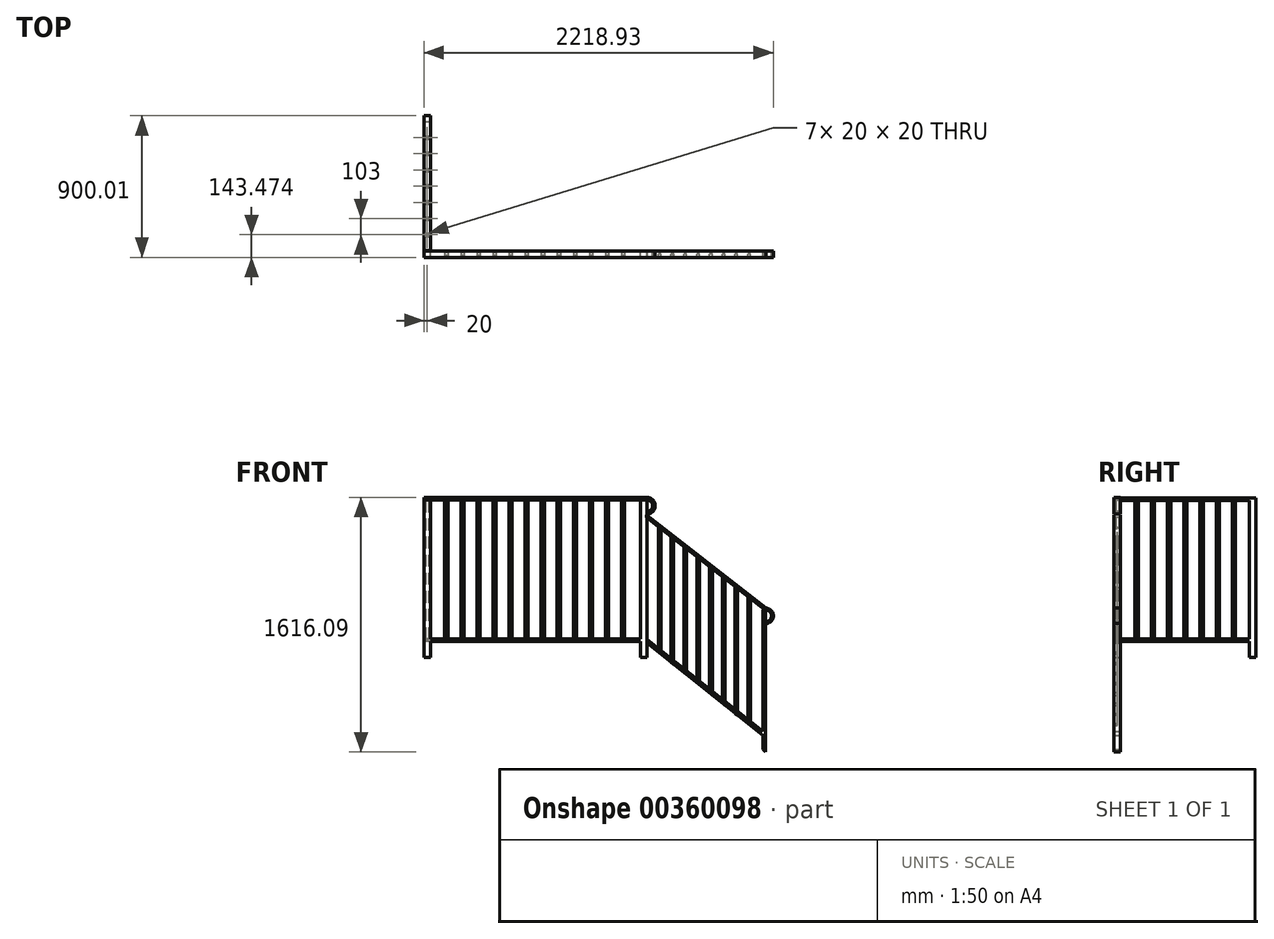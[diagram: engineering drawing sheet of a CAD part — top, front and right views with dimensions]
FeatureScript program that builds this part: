
annotation { "Feature Type Name" : "Feature", "Feature Type Description" : "" }
export const myFeature = defineFeature(function(context is Context, id is Id, definition is map)
    precondition{}
    {
        {
            var Q0;
            Q0=qCreatedBy(makeId("Front.planeOp"),FACE);
            var sketch = newSketch(context, id + "F0", { "sketchPlane" : qUnion([Q0])});
            skLineSegment(sketch, "E0", {"start": v(1415, 600.1) * mm, "end": v(1415, 1600.1) * mm});
            skLineSegment(sketch, "E1", {"start": v(1415, 1600.1) * mm, "end": v(1375, 1600.1) * mm});
            skLineSegment(sketch, "E2", {"start": v(1375, 1600.1) * mm, "end": v(1375, 600.14) * mm});
            skLineSegment(sketch, "E3", {"start": v(1375, 600.14) * mm, "end": v(1415, 600.1) * mm});
            skLineSegment(sketch, "E4.bottom", {"start": v(0, 600.1) * mm, "end": v(40, 600.1) * mm});
            skLineSegment(sketch, "E4.top", {"start": v(0, 1600.1) * mm, "end": v(40, 1600.1) * mm});
            skLineSegment(sketch, "E4.left", {"start": v(0, 600.1) * mm, "end": v(0, 1600.1) * mm});
            skLineSegment(sketch, "E4.right", {"start": v(40, 600.1) * mm, "end": v(40, 1600.1) * mm});
            skLineSegment(sketch, "E5", {"start": v(40, 600.1) * mm, "end": v(40, 700.1) * mm});
            skLineSegment(sketch, "E6", {"start": v(40, 700.1) * mm, "end": v(1375, 700.1) * mm});
            skLineSegment(sketch, "E7", {"start": v(1375, 700.1) * mm, "end": v(1375, 716.1) * mm});
            skLineSegment(sketch, "E8", {"start": v(1375, 716.1) * mm, "end": v(40, 716.1) * mm});
            skLineSegment(sketch, "E9", {"start": v(40, 716.1) * mm, "end": v(40, 700.1) * mm});
            skSolve(sketch);
        }
        {
            var Q0;
            Q0 = qSketchRegion(id + "F0", true);
            extrude(context, id + "F1", {"entities" : qUnion([Q0]), "endBound" : BoundingType.SYMMETRIC, "depth" : 40 * mm});
        }
        {
            var Q0;
            Q0=makeQuery(id+"F1.opExtrude","SWEPT_FACE",FACE,{"disambiguationData":[OSD([sQuery(id+"F0.wireOp",EDGE,"E4.left")])]});
            var sketch = newSketch(context, id + "F2", { "sketchPlane" : qUnion([Q0])});
            skLineSegment(sketch, "E10.bottom", {"start": v(-20, 1600.1) * mm, "end": v(20, 1600.1) * mm});
            skLineSegment(sketch, "E10.top", {"start": v(-20, 1616.1) * mm, "end": v(20, 1616.1) * mm});
            skLineSegment(sketch, "E10.left", {"start": v(-20, 1600.1) * mm, "end": v(-20, 1616.1) * mm});
            skLineSegment(sketch, "E10.right", {"start": v(20, 1600.1) * mm, "end": v(20, 1616.1) * mm});
            skSolve(sketch);
        }
        {
            var Q0;
            Q0=makeQuery(id+"F2.imprint","IMPRINT",FACE,{"disambiguationData":[TD([[makeQuery(id+"F2.imprint","IMPRINT",EDGE,{"derivedFrom":sQuery(id+"F2.wireOp",EDGE,"E10.bottom")}),-1.0]])]});
            var sketch = newSketch(context, id + "F3", { "sketchPlane" : qUnion([Q0])});
            skLineSegment(sketch, "E11.bottom", {"start": v(-20, 1600.2) * mm, "end": v(20, 1600.2) * mm});
            skLineSegment(sketch, "E11.top", {"start": v(-20, 1616.2) * mm, "end": v(20, 1616.2) * mm});
            skLineSegment(sketch, "E11.left", {"start": v(-20, 1600.2) * mm, "end": v(-20, 1616.2) * mm});
            skLineSegment(sketch, "E11.right", {"start": v(20, 1600.2) * mm, "end": v(20, 1616.2) * mm});
            skPoint(sketch, "E11.middle", {"position": v(0, 1608.2) * mm});
            skSolve(sketch);
        }
        {
            var Q0;
            Q0=qCreatedBy(makeId("Front.planeOp"),FACE);
            var sketch = newSketch(context, id + "F4", { "sketchPlane" : qUnion([Q0])});
            skLineSegment(sketch, "E12", {"start": v(0, 1608.38) * mm, "end": v(1415.74, 1608.38) * mm});
            skArc(sketch, "E13", {"start": v(1415.74, 1518.38) * mm, "mid": v(1460.74, 1563.38) * mm, "end": v(1415.74, 1608.38) * mm});
            skSolve(sketch);
        }
        {
            var Q0;
            {var subQ0=sQuery(id+"F3.wireOp",EDGE,"E11.left");var subQ1=sQuery(id+"F3.wireOp",EDGE,"E11.bottom");var subQ2=makeQuery(id+"F3.imprint","INTERSECT",VERTEX,{"derivedFrom":[subQ1,subQ0]});Q0=makeQuery(id+"F3.imprint","IMPRINT",FACE,{"disambiguationData":[TD([[makeQuery(id+"F3.imprint","IMPRINT",EDGE,{"disambiguationData":[TD([[subQ2,-1.0]])],"derivedFrom":subQ1}),1.0]])]});}
            var Q1;
            Q1=sQuery(id+"F4.wireOp",EDGE,"E12");
            var Q2;
            Q2=sQuery(id+"F4.wireOp",EDGE,"E13");
            sweep(context, id + "F5", {"profiles" : qUnion([Q0]), "path" : qUnion([Q1, Q2])});
        }
        {
            var Q0;
            Q0=qCreatedBy(makeId("Front.planeOp"),FACE);
            var sketch = newSketch(context, id + "F6", { "sketchPlane" : qUnion([Q0])});
            skLineSegment(sketch, "E14", {"start": v(2169.22, 0) * mm, "end": v(2169.22, 900) * mm});
            skLineSegment(sketch, "E15", {"start": v(1415.57, 1482.12) * mm, "end": v(1415.57, 1502.33) * mm});
            skLineSegment(sketch, "E16", {"start": v(2169.22, 900) * mm, "end": v(2153.22, 900) * mm});
            skLineSegment(sketch, "E17", {"start": v(2153.22, 900) * mm, "end": v(2153.22, 15.7) * mm});
            skLineSegment(sketch, "E18", {"start": v(2153.22, 15.7) * mm, "end": v(2169.22, 0) * mm});
            skLineSegment(sketch, "E19", {"start": v(1415.57, 692.8) * mm, "end": v(2153.22, 103.74) * mm});
            skLineSegment(sketch, "E20", {"start": v(1415.18, 712.76) * mm, "end": v(2153.22, 128.7) * mm});
            skLineSegment(sketch, "E21", {"start": v(1415.18, 712.76) * mm, "end": v(1415.57, 692.8) * mm});
            skSolve(sketch);
        }
        {
            var Q0;
            Q0 = qSketchRegion(id + "F6", true);
            extrude(context, id + "F7", {"entities" : qUnion([Q0]), "endBound" : BoundingType.SYMMETRIC, "depth" : 40 * mm});
        }
        {
            var Q0;
            Q0=makeQuery(id+"F1.opExtrude","SWEPT_FACE",FACE,{"disambiguationData":[OSD([sQuery(id+"F0.wireOp",EDGE,"E0")])]});
            var sketch = newSketch(context, id + "F8", { "sketchPlane" : qUnion([Q0])});
            skLineSegment(sketch, "E22.bottom", {"start": v(20, 1486.8) * mm, "end": v(-20, 1486.8) * mm});
            skLineSegment(sketch, "E22.top", {"start": v(20, 1502.8) * mm, "end": v(-20, 1502.8) * mm});
            skLineSegment(sketch, "E22.left", {"start": v(20, 1486.8) * mm, "end": v(20, 1502.8) * mm});
            skLineSegment(sketch, "E22.right", {"start": v(-20, 1486.8) * mm, "end": v(-20, 1502.8) * mm});
            skPoint(sketch, "E22.middle", {"position": v(0, 1494.8) * mm});
            skSolve(sketch);
        }
        {
            var Q0;
            Q0=qCreatedBy(makeId("Front.planeOp"),FACE);
            var sketch = newSketch(context, id + "F9", { "sketchPlane" : qUnion([Q0])});
            skLineSegment(sketch, "E23", {"start": v(2169.44, 908.95) * mm, "end": v(1413.58, 1498.8) * mm});
            skArc(sketch, "E24", {"start": v(2169.44, 818.95) * mm, "mid": v(2214.81, 863.95) * mm, "end": v(2169.44, 908.95) * mm});
            skSolve(sketch);
        }
        {
            var Q0;
            Q0=makeQuery(id+"F8.imprint","IMPRINT",FACE,{"disambiguationData":[TD([[makeQuery(id+"F8.imprint","IMPRINT",EDGE,{"derivedFrom":sQuery(id+"F8.wireOp",EDGE,"E22.bottom")}),-1.0]])]});
            var Q1;
            Q1=sQuery(id+"F9.wireOp",EDGE,"E23");
            var Q2;
            Q2=sQuery(id+"F9.wireOp",EDGE,"E24");
            sweep(context, id + "F10", {"profiles" : qUnion([Q0]), "path" : qUnion([Q1, Q2])});
        }
        {
            var Q0;
            Q0=makeQuery(id+"F1.opExtrude","SWEPT_FACE",FACE,{"disambiguationData":[OSD([sQuery(id+"F0.wireOp",EDGE,"E6")])]});
            var sketch = newSketch(context, id + "F11", { "sketchPlane" : qUnion([Q0])});
            skLineSegment(sketch, "E25", {"start": v(40, 0) * mm, "end": v(142, 0) * mm});
            skPoint(sketch, "E25.endSnap0", {"position": v(40, 0) * mm});
            skLineSegment(sketch, "E26", {"start": v(142, 0) * mm, "end": v(244, 0) * mm});
            skLineSegment(sketch, "E27", {"start": v(244, 0) * mm, "end": v(346, 0) * mm});
            skLineSegment(sketch, "E28", {"start": v(346, 0) * mm, "end": v(448, 0) * mm});
            skLineSegment(sketch, "E29", {"start": v(448, 0) * mm, "end": v(550, 0) * mm});
            skLineSegment(sketch, "E30", {"start": v(550, 0) * mm, "end": v(652, 0) * mm});
            skLineSegment(sketch, "E31", {"start": v(652, 0) * mm, "end": v(754, 0) * mm});
            skLineSegment(sketch, "E32", {"start": v(754, 0) * mm, "end": v(856, 0) * mm});
            skLineSegment(sketch, "E33", {"start": v(856, 0) * mm, "end": v(958, 0) * mm});
            skLineSegment(sketch, "E34", {"start": v(958, 0) * mm, "end": v(1060, 0) * mm});
            skLineSegment(sketch, "E35", {"start": v(1060, 0) * mm, "end": v(1162, 0) * mm});
            skLineSegment(sketch, "E36", {"start": v(1162, 0) * mm, "end": v(1264, 0) * mm});
            skLineSegment(sketch, "E37.bottom", {"start": v(152, -10) * mm, "end": v(132, -10) * mm});
            skLineSegment(sketch, "E37.top", {"start": v(152, 10) * mm, "end": v(132, 10) * mm});
            skLineSegment(sketch, "E37.left", {"start": v(152, -10) * mm, "end": v(152, 10) * mm});
            skLineSegment(sketch, "E37.right", {"start": v(132, -10) * mm, "end": v(132, 10) * mm});
            skPoint(sketch, "E37.middle", {"position": v(142, 0) * mm});
            skLineSegment(sketch, "E38.bottom", {"start": v(254, -10) * mm, "end": v(234, -10) * mm});
            skLineSegment(sketch, "E38.top", {"start": v(254, 10) * mm, "end": v(234, 10) * mm});
            skLineSegment(sketch, "E38.left", {"start": v(254, -10) * mm, "end": v(254, 10) * mm});
            skLineSegment(sketch, "E38.right", {"start": v(234, -10) * mm, "end": v(234, 10) * mm});
            skPoint(sketch, "E38.middle", {"position": v(244, 0) * mm});
            skLineSegment(sketch, "E39.bottom", {"start": v(356, -10) * mm, "end": v(336, -10) * mm});
            skLineSegment(sketch, "E39.top", {"start": v(356, 10) * mm, "end": v(336, 10) * mm});
            skLineSegment(sketch, "E39.left", {"start": v(356, -10) * mm, "end": v(356, 10) * mm});
            skLineSegment(sketch, "E39.right", {"start": v(336, -10) * mm, "end": v(336, 10) * mm});
            skPoint(sketch, "E39.middle", {"position": v(346, 0) * mm});
            skLineSegment(sketch, "E40.bottom", {"start": v(458, -10) * mm, "end": v(438, -10) * mm});
            skLineSegment(sketch, "E40.top", {"start": v(458, 10) * mm, "end": v(438, 10) * mm});
            skLineSegment(sketch, "E40.left", {"start": v(458, -10) * mm, "end": v(458, 10) * mm});
            skLineSegment(sketch, "E40.right", {"start": v(438, -10) * mm, "end": v(438, 10) * mm});
            skPoint(sketch, "E40.middle", {"position": v(448, 0) * mm});
            skLineSegment(sketch, "E41.bottom", {"start": v(560, -10) * mm, "end": v(540, -10) * mm});
            skLineSegment(sketch, "E41.top", {"start": v(560, 10) * mm, "end": v(540, 10) * mm});
            skLineSegment(sketch, "E41.left", {"start": v(560, -10) * mm, "end": v(560, 10) * mm});
            skLineSegment(sketch, "E41.right", {"start": v(540, -10) * mm, "end": v(540, 10) * mm});
            skPoint(sketch, "E41.middle", {"position": v(550, 0) * mm});
            skLineSegment(sketch, "E42.bottom", {"start": v(662, -10) * mm, "end": v(642, -10) * mm});
            skLineSegment(sketch, "E42.top", {"start": v(662, 10) * mm, "end": v(642, 10) * mm});
            skLineSegment(sketch, "E42.left", {"start": v(662, -10) * mm, "end": v(662, 10) * mm});
            skLineSegment(sketch, "E42.right", {"start": v(642, -10) * mm, "end": v(642, 10) * mm});
            skPoint(sketch, "E42.middle", {"position": v(652, 0) * mm});
            skLineSegment(sketch, "E43.bottom", {"start": v(764, -10) * mm, "end": v(744, -10) * mm});
            skLineSegment(sketch, "E43.top", {"start": v(764, 10) * mm, "end": v(744, 10) * mm});
            skLineSegment(sketch, "E43.left", {"start": v(764, -10) * mm, "end": v(764, 10) * mm});
            skLineSegment(sketch, "E43.right", {"start": v(744, -10) * mm, "end": v(744, 10) * mm});
            skPoint(sketch, "E43.middle", {"position": v(754, 0) * mm});
            skLineSegment(sketch, "E44.bottom", {"start": v(866, -10) * mm, "end": v(846, -10) * mm});
            skLineSegment(sketch, "E44.top", {"start": v(866, 10) * mm, "end": v(846, 10) * mm});
            skLineSegment(sketch, "E44.left", {"start": v(866, -10) * mm, "end": v(866, 10) * mm});
            skLineSegment(sketch, "E44.right", {"start": v(846, -10) * mm, "end": v(846, 10) * mm});
            skPoint(sketch, "E44.middle", {"position": v(856, 0) * mm});
            skLineSegment(sketch, "E45.bottom", {"start": v(968, -10) * mm, "end": v(948, -10) * mm});
            skLineSegment(sketch, "E45.top", {"start": v(968, 10) * mm, "end": v(948, 10) * mm});
            skLineSegment(sketch, "E45.left", {"start": v(968, -10) * mm, "end": v(968, 10) * mm});
            skLineSegment(sketch, "E45.right", {"start": v(948, -10) * mm, "end": v(948, 10) * mm});
            skPoint(sketch, "E45.middle", {"position": v(958, 0) * mm});
            skPoint(sketch, "E46.middle", {"position": v(1060, 0) * mm});
            skLineSegment(sketch, "E47.bottom", {"start": v(1070, -10) * mm, "end": v(1050, -10) * mm});
            skLineSegment(sketch, "E47.top", {"start": v(1070, 10) * mm, "end": v(1050, 10) * mm});
            skLineSegment(sketch, "E47.left", {"start": v(1070, -10) * mm, "end": v(1070, 10) * mm});
            skLineSegment(sketch, "E47.right", {"start": v(1050, -10) * mm, "end": v(1050, 10) * mm});
            skLineSegment(sketch, "E48.bottom", {"start": v(1172, -10) * mm, "end": v(1152, -10) * mm});
            skLineSegment(sketch, "E48.top", {"start": v(1172, 10) * mm, "end": v(1152, 10) * mm});
            skLineSegment(sketch, "E48.left", {"start": v(1172, -10) * mm, "end": v(1172, 10) * mm});
            skLineSegment(sketch, "E48.right", {"start": v(1152, -10) * mm, "end": v(1152, 10) * mm});
            skPoint(sketch, "E48.middle", {"position": v(1162, 0) * mm});
            skLineSegment(sketch, "E49.bottom", {"start": v(1274, -10) * mm, "end": v(1254, -10) * mm});
            skLineSegment(sketch, "E49.top", {"start": v(1274, 10) * mm, "end": v(1254, 10) * mm});
            skLineSegment(sketch, "E49.left", {"start": v(1274, -10) * mm, "end": v(1274, 10) * mm});
            skLineSegment(sketch, "E49.right", {"start": v(1254, -10) * mm, "end": v(1254, 10) * mm});
            skPoint(sketch, "E49.middle", {"position": v(1264, 0) * mm});
            skSolve(sketch);
        }
        {
            var Q0;
            Q0 = qSketchRegion(id + "F11", true);
            extrude(context, id + "F12", {"entities" : qUnion([Q0]), "oppositeDirection" : true, "depth" : 905 * mm});
        }
        {
            var Q0;
            Q0=qCreatedBy(makeId("Front.planeOp"),FACE);
            var sketch = newSketch(context, id + "F13", { "sketchPlane" : qUnion([Q0])});
            skLineSegment(sketch, "E50", {"start": v(1489.6, 633.32) * mm, "end": v(1489.6, 1429.3) * mm});
            skLineSegment(sketch, "E51", {"start": v(1504.3, 620.7) * mm, "end": v(1504.3, 1417.72) * mm});
            skLineSegment(sketch, "E52", {"start": v(1569.3, 568.65) * mm, "end": v(1569.3, 1361.75) * mm});
            skLineSegment(sketch, "E53", {"start": v(1585.39, 555.75) * mm, "end": v(1585.39, 1345.38) * mm});
            skLineSegment(sketch, "E54", {"start": v(1649.77, 505.44) * mm, "end": v(1649.77, 1302.64) * mm});
            skLineSegment(sketch, "E55", {"start": v(1667.4, 491.46) * mm, "end": v(1667.4, 1288.96) * mm});
            skLineSegment(sketch, "E56", {"start": v(1732.41, 440.66) * mm, "end": v(1732.41, 1239) * mm});
            skLineSegment(sketch, "E57", {"start": v(1748.8, 427.08) * mm, "end": v(1748.8, 1225.67) * mm});
            skLineSegment(sketch, "E58", {"start": v(1812.2, 377.07) * mm, "end": v(1812.2, 1175.59) * mm});
            skLineSegment(sketch, "E59", {"start": v(1831.2, 359.05) * mm, "end": v(1831.2, 1161.81) * mm});
            skLineSegment(sketch, "E60", {"start": v(1895.34, 310.04) * mm, "end": v(1895.34, 1111.73) * mm});
            skLineSegment(sketch, "E61", {"start": v(1910.53, 294.03) * mm, "end": v(1910.53, 1100.16) * mm});
            skLineSegment(sketch, "E62", {"start": v(1976.52, 244.01) * mm, "end": v(1976.52, 1056.94) * mm});
            skLineSegment(sketch, "E63", {"start": v(1991.48, 233.33) * mm, "end": v(1991.48, 1038.46) * mm});
            skLineSegment(sketch, "E64", {"start": v(2056.38, 180.6) * mm, "end": v(2056.38, 985.83) * mm});
            skLineSegment(sketch, "E65", {"start": v(2073.41, 167.22) * mm, "end": v(2073.41, 970.02) * mm});
            skLineSegment(sketch, "E66", {"start": v(2073.41, 970.02) * mm, "end": v(2056.38, 985.83) * mm});
            skLineSegment(sketch, "E67", {"start": v(2073.41, 167.22) * mm, "end": v(2056.38, 180.6) * mm});
            skLineSegment(sketch, "E68", {"start": v(1991.48, 233.33) * mm, "end": v(1976.52, 244.01) * mm});
            skLineSegment(sketch, "E69", {"start": v(1910.53, 294.03) * mm, "end": v(1895.34, 310.04) * mm});
            skLineSegment(sketch, "E70", {"start": v(1831.2, 359.05) * mm, "end": v(1812.2, 377.07) * mm});
            skLineSegment(sketch, "E71", {"start": v(1748.8, 427.08) * mm, "end": v(1732.41, 440.66) * mm});
            skLineSegment(sketch, "E72", {"start": v(1667.4, 491.46) * mm, "end": v(1649.77, 505.44) * mm});
            skLineSegment(sketch, "E73", {"start": v(1585.39, 555.75) * mm, "end": v(1569.3, 568.65) * mm});
            skLineSegment(sketch, "E74", {"start": v(1504.3, 620.7) * mm, "end": v(1489.6, 633.32) * mm});
            skLineSegment(sketch, "E75", {"start": v(1489.6, 1429.3) * mm, "end": v(1504.3, 1417.72) * mm});
            skLineSegment(sketch, "E76", {"start": v(1569.3, 1361.75) * mm, "end": v(1569.3, 1366.2) * mm});
            skLineSegment(sketch, "E77", {"start": v(1569.3, 1366.2) * mm, "end": v(1586.21, 1353.12) * mm});
            skLineSegment(sketch, "E78", {"start": v(1586.21, 1353.12) * mm, "end": v(1585.39, 1345.38) * mm});
            skLineSegment(sketch, "E79", {"start": v(1649.77, 1302.64) * mm, "end": v(1667.4, 1288.96) * mm});
            skLineSegment(sketch, "E80", {"start": v(1976.52, 1048.09) * mm, "end": v(1991.48, 1038.46) * mm});
            skLineSegment(sketch, "E81", {"start": v(1895.34, 1111.73) * mm, "end": v(1910.53, 1100.16) * mm});
            skLineSegment(sketch, "E82", {"start": v(1831.2, 1161.81) * mm, "end": v(1812.2, 1175.59) * mm});
            skLineSegment(sketch, "E83", {"start": v(1748.8, 1225.67) * mm, "end": v(1732.41, 1239) * mm});
            skSolve(sketch);
        }
        {
            var Q0;
            Q0 = qSketchRegion(id + "F13", true);
            extrude(context, id + "F14", {"entities" : qUnion([Q0]), "depth" : 20 * mm});
        }
        {
            var Q0;
            Q0=makeQuery(id+"F2.imprint","IMPRINT",FACE,{"disambiguationData":[TD([[makeQuery(id+"F2.imprint","IMPRINT",EDGE,{"derivedFrom":sQuery(id+"F2.wireOp",EDGE,"E10.bottom")}),1.0]])]});
            var sketch = newSketch(context, id + "F15", { "sketchPlane" : qUnion([Q0])});
            skLineSegment(sketch, "E84", {"start": v(-20, 600.85) * mm, "end": v(-880, 600.85) * mm});
            skLineSegment(sketch, "E85", {"start": v(-880, 600.85) * mm, "end": v(-880, 1596.85) * mm});
            skLineSegment(sketch, "E86", {"start": v(-880, 1596.85) * mm, "end": v(-840, 1596.85) * mm});
            skLineSegment(sketch, "E87", {"start": v(-840, 1596.85) * mm, "end": v(-840, 600.85) * mm});
            skLineSegment(sketch, "E88", {"start": v(-840, 600.85) * mm, "end": v(-880, 600.85) * mm});
            skLineSegment(sketch, "E89.bottom", {"start": v(-24.05, 1612.85) * mm, "end": v(-880, 1612.85) * mm});
            skLineSegment(sketch, "E89.top", {"start": v(-24.05, 1596.85) * mm, "end": v(-880, 1596.85) * mm});
            skLineSegment(sketch, "E89.left", {"start": v(-24.05, 1612.85) * mm, "end": v(-24.05, 1596.85) * mm});
            skLineSegment(sketch, "E89.right", {"start": v(-880, 1612.85) * mm, "end": v(-880, 1596.85) * mm});
            skLineSegment(sketch, "E90", {"start": v(-840, 600.85) * mm, "end": v(-840, 700.85) * mm});
            skLineSegment(sketch, "E91", {"start": v(-840, 700.85) * mm, "end": v(-20.47, 700.85) * mm});
            skLineSegment(sketch, "E92", {"start": v(-20.47, 700.85) * mm, "end": v(-20.47, 716.85) * mm});
            skLineSegment(sketch, "E93", {"start": v(-20.47, 716.85) * mm, "end": v(-840, 716.85) * mm});
            skLineSegment(sketch, "E94", {"start": v(-840, 716.85) * mm, "end": v(-840, 700.85) * mm});
            skSolve(sketch);
        }
        {
            var Q0;
            Q0=makeQuery(id+"F15.imprint","IMPRINT",FACE,{"disambiguationData":[TD([[makeQuery(id+"F15.imprint","IMPRINT",EDGE,{"derivedFrom":sQuery(id+"F15.wireOp",EDGE,"E85")}),-1.0]])]});
            extrude(context, id + "F16", {"entities" : qUnion([Q0]), "oppositeDirection" : true, "depth" : 40 * mm});
        }
        {
            var Q0;
            Q0 = qSketchRegion(id + "F15", true);
            extrude(context, id + "F17", {"entities" : qUnion([Q0]), "operationType" : NewBodyOperationType.ADD, "oppositeDirection" : true, "depth" : 40 * mm});
        }
        {
            var Q0;
            Q0=makeQuery(id+"F17.opExtrude","SWEPT_FACE",FACE,{"disambiguationData":[OSD([sQuery(id+"F15.wireOp",EDGE,"E91")])]});
            var sketch = newSketch(context, id + "F18", { "sketchPlane" : qUnion([Q0])});
            skLineSegment(sketch, "E95", {"start": v(20, -20.47) * mm, "end": v(20, -123.47) * mm});
            skLineSegment(sketch, "E96", {"start": v(20, -123.47) * mm, "end": v(20, -226.47) * mm});
            skLineSegment(sketch, "E97", {"start": v(20, -226.47) * mm, "end": v(20, -329.47) * mm});
            skLineSegment(sketch, "E98", {"start": v(20, -329.47) * mm, "end": v(20, -432.47) * mm});
            skLineSegment(sketch, "E99", {"start": v(20, -432.47) * mm, "end": v(20, -535.47) * mm});
            skLineSegment(sketch, "E100", {"start": v(20, -535.47) * mm, "end": v(20, -638.47) * mm});
            skLineSegment(sketch, "E101", {"start": v(20, -638.47) * mm, "end": v(20, -741.47) * mm});
            skLineSegment(sketch, "E102.bottom", {"start": v(30, -133.47) * mm, "end": v(10, -133.47) * mm});
            skLineSegment(sketch, "E102.top", {"start": v(30, -113.47) * mm, "end": v(10, -113.47) * mm});
            skLineSegment(sketch, "E102.left", {"start": v(30, -133.47) * mm, "end": v(30, -113.47) * mm});
            skLineSegment(sketch, "E102.right", {"start": v(10, -133.47) * mm, "end": v(10, -113.47) * mm});
            skPoint(sketch, "E102.middle", {"position": v(20, -123.47) * mm});
            skLineSegment(sketch, "E103.bottom", {"start": v(30, -236.47) * mm, "end": v(10, -236.47) * mm});
            skLineSegment(sketch, "E103.top", {"start": v(30, -216.47) * mm, "end": v(10, -216.47) * mm});
            skLineSegment(sketch, "E103.left", {"start": v(30, -236.47) * mm, "end": v(30, -216.47) * mm});
            skLineSegment(sketch, "E103.right", {"start": v(10, -236.47) * mm, "end": v(10, -216.47) * mm});
            skPoint(sketch, "E103.middle", {"position": v(20, -226.47) * mm});
            skLineSegment(sketch, "E104.bottom", {"start": v(30, -339.47) * mm, "end": v(10, -339.47) * mm});
            skLineSegment(sketch, "E104.top", {"start": v(30, -319.47) * mm, "end": v(10, -319.47) * mm});
            skLineSegment(sketch, "E104.left", {"start": v(30, -339.47) * mm, "end": v(30, -319.47) * mm});
            skLineSegment(sketch, "E104.right", {"start": v(10, -339.47) * mm, "end": v(10, -319.47) * mm});
            skPoint(sketch, "E104.middle", {"position": v(20, -329.47) * mm});
            skLineSegment(sketch, "E105.bottom", {"start": v(30, -442.47) * mm, "end": v(10, -442.47) * mm});
            skLineSegment(sketch, "E105.top", {"start": v(30, -422.47) * mm, "end": v(10, -422.47) * mm});
            skLineSegment(sketch, "E105.left", {"start": v(30, -442.47) * mm, "end": v(30, -422.47) * mm});
            skLineSegment(sketch, "E105.right", {"start": v(10, -442.47) * mm, "end": v(10, -422.47) * mm});
            skPoint(sketch, "E105.middle", {"position": v(20, -432.47) * mm});
            skLineSegment(sketch, "E106.bottom", {"start": v(30, -545.47) * mm, "end": v(10, -545.47) * mm});
            skLineSegment(sketch, "E106.top", {"start": v(30, -525.47) * mm, "end": v(10, -525.47) * mm});
            skLineSegment(sketch, "E106.left", {"start": v(30, -545.47) * mm, "end": v(30, -525.47) * mm});
            skLineSegment(sketch, "E106.right", {"start": v(10, -545.47) * mm, "end": v(10, -525.47) * mm});
            skPoint(sketch, "E106.middle", {"position": v(20, -535.47) * mm});
            skLineSegment(sketch, "E107.bottom", {"start": v(30, -648.47) * mm, "end": v(10, -648.47) * mm});
            skLineSegment(sketch, "E107.top", {"start": v(30, -628.47) * mm, "end": v(10, -628.47) * mm});
            skLineSegment(sketch, "E107.left", {"start": v(30, -648.47) * mm, "end": v(30, -628.47) * mm});
            skLineSegment(sketch, "E107.right", {"start": v(10, -648.47) * mm, "end": v(10, -628.47) * mm});
            skPoint(sketch, "E107.middle", {"position": v(20, -638.47) * mm});
            skLineSegment(sketch, "E108.bottom", {"start": v(30, -751.47) * mm, "end": v(10, -751.47) * mm});
            skLineSegment(sketch, "E108.top", {"start": v(30, -731.47) * mm, "end": v(10, -731.47) * mm});
            skLineSegment(sketch, "E108.left", {"start": v(30, -751.47) * mm, "end": v(30, -731.47) * mm});
            skLineSegment(sketch, "E108.right", {"start": v(10, -751.47) * mm, "end": v(10, -731.47) * mm});
            skPoint(sketch, "E108.middle", {"position": v(20, -741.47) * mm});
            skSolve(sketch);
        }
        {
            var Q0;
            Q0 = qSketchRegion(id + "F18", true);
            extrude(context, id + "F19", {"entities" : qUnion([Q0]), "operationType" : NewBodyOperationType.ADD, "oppositeDirection" : true, "depth" : 900 * mm});
        }
    });
